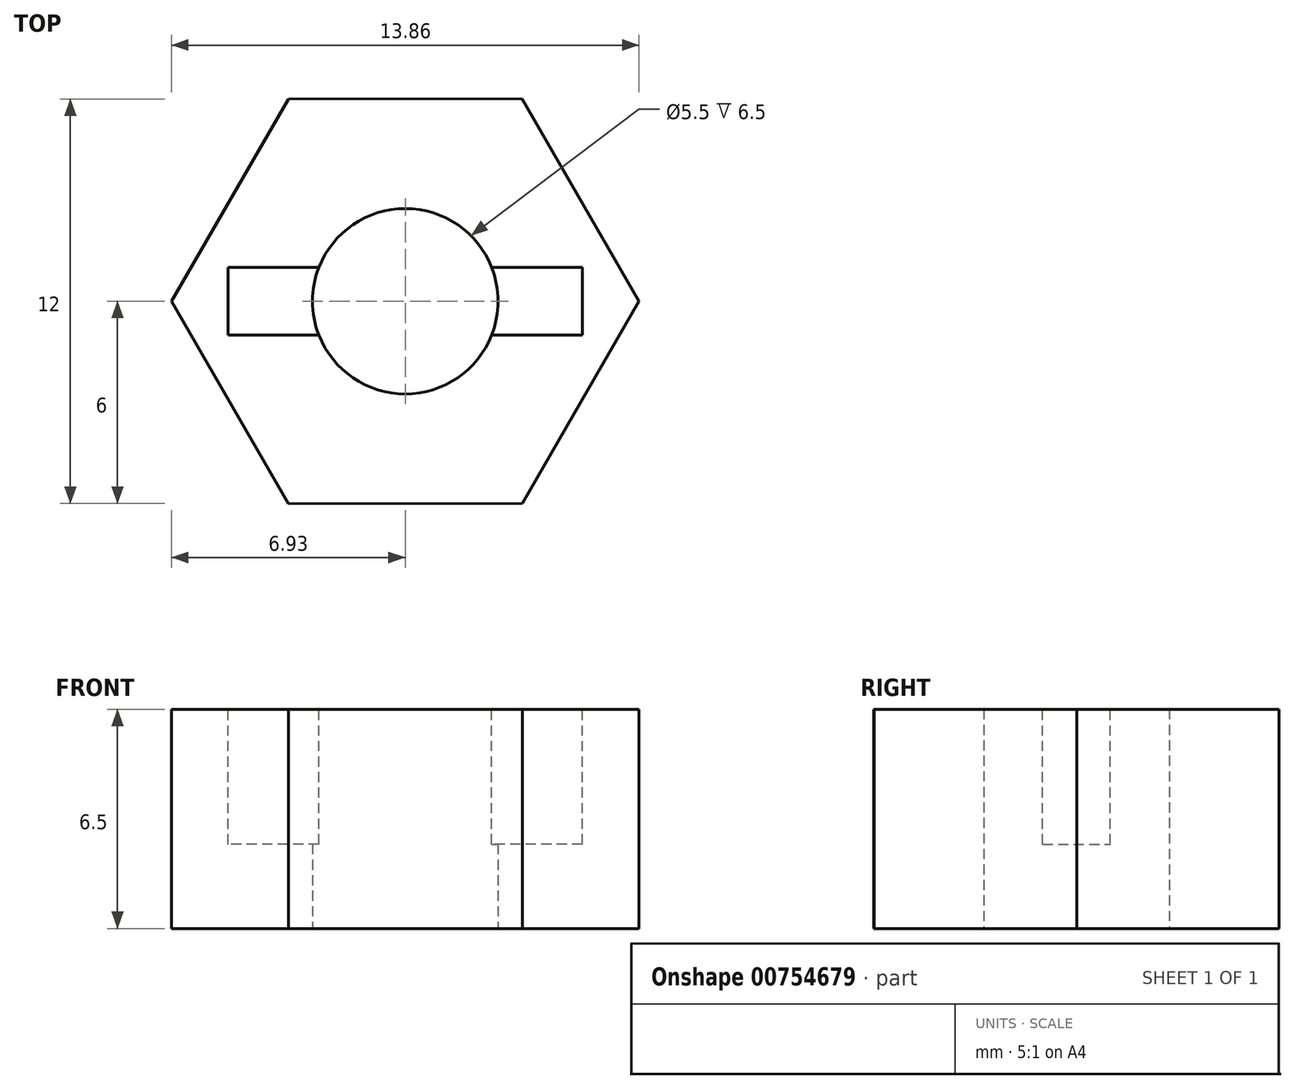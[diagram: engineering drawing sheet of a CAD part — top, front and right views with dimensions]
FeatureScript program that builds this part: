
annotation { "Feature Type Name" : "Feature", "Feature Type Description" : "" }
export const myFeature = defineFeature(function(context is Context, id is Id, definition is map)
    precondition{}
    {
        {
            var Q0;
            Q0=qCreatedBy(makeId("Top.planeOp"),FACE);
            var sketch = newSketch(context, id + "F0", { "sketchPlane" : qUnion([Q0])});
            skCircle(sketch, "E0.cCircle", {"center": v(0, 0) * mm, "radius": 6 * mm, "construction": true});
            skLineSegment(sketch, "E0.0", {"start": v(6.93, 0) * mm, "end": v(3.47, -6) * mm});
            skLineSegment(sketch, "E0.1", {"start": v(3.47, -6) * mm, "end": v(-3.46, -6) * mm});
            skLineSegment(sketch, "E0.2", {"start": v(-3.46, -6) * mm, "end": v(-6.93, 0) * mm});
            skLineSegment(sketch, "E0.3", {"start": v(-6.93, 0) * mm, "end": v(-3.47, 6) * mm});
            skLineSegment(sketch, "E0.4", {"start": v(-3.47, 6) * mm, "end": v(3.46, 6) * mm});
            skLineSegment(sketch, "E0.5", {"start": v(3.46, 6) * mm, "end": v(6.93, 0) * mm});
            skPoint(sketch, "E0.0.midPoint", {"position": v(5.2, -3) * mm});
            skCircle(sketch, "E1", {"center": v(0, 0) * mm, "radius": 2.75 * mm});
            skSolve(sketch);
        }
        {
            var Q0;
            Q0=makeQuery(id+"F0.imprint","IMPRINT",FACE,{"disambiguationData":[TD([[makeQuery(id+"F0.imprint","IMPRINT",EDGE,{"derivedFrom":sQuery(id+"F0.wireOp",EDGE,"E0.0")}),-1.0]])]});
            extrude(context, id + "F1", {"entities" : qUnion([Q0]), "depth" : 6.5 * mm, "offsetDistance" : 25 * mm});
        }
        {
            var Q0;
            Q0=makeQuery(id+"F1.opExtrude","CAP_FACE",FACE,{"disambiguationData":[OSD([sQuery(id+"F0.wireOp",EDGE,"E0.0"),sQuery(id+"F0.wireOp",EDGE,"E0.1"),sQuery(id+"F0.wireOp",EDGE,"E0.2"),sQuery(id+"F0.wireOp",EDGE,"E0.3"),sQuery(id+"F0.wireOp",EDGE,"E0.4"),sQuery(id+"F0.wireOp",EDGE,"E0.5"),sQuery(id+"F0.wireOp",EDGE,"E1")])],"isStart":false});
            var sketch = newSketch(context, id + "F2", { "sketchPlane" : qUnion([Q0])});
            skLineSegment(sketch, "E2.bottom", {"start": v(5.25, -1) * mm, "end": v(-5.25, -1) * mm});
            skLineSegment(sketch, "E2.top", {"start": v(5.25, 1) * mm, "end": v(-5.25, 1) * mm});
            skLineSegment(sketch, "E2.left", {"start": v(5.25, -1) * mm, "end": v(5.25, 1) * mm});
            skLineSegment(sketch, "E2.right", {"start": v(-5.25, -1) * mm, "end": v(-5.25, 1) * mm});
            skPoint(sketch, "E2.middle", {"position": v(0, 0) * mm});
            skSolve(sketch);
        }
        {
            var Q0;
            {var subQ0=sQuery(id+"F2.wireOp",EDGE,"E2.right");Q0=makeQuery(id+"F2.imprint","IMPRINT",FACE,{"disambiguationData":[TD([[makeQuery(id+"F2.imprint","IMPRINT",EDGE,{"derivedFrom":subQ0}),-1.0]])]});}
            var Q1;
            {var subQ0=sQuery(id+"F2.wireOp",EDGE,"E2.left");Q1=makeQuery(id+"F2.imprint","IMPRINT",FACE,{"disambiguationData":[TD([[makeQuery(id+"F2.imprint","IMPRINT",EDGE,{"derivedFrom":subQ0}),1.0]])]});}
            extrude(context, id + "F3", {"entities" : qUnion([Q0, Q1]), "operationType" : NewBodyOperationType.REMOVE, "oppositeDirection" : true, "depth" : 4 * mm, "offsetDistance" : 25 * mm});
        }
    });
